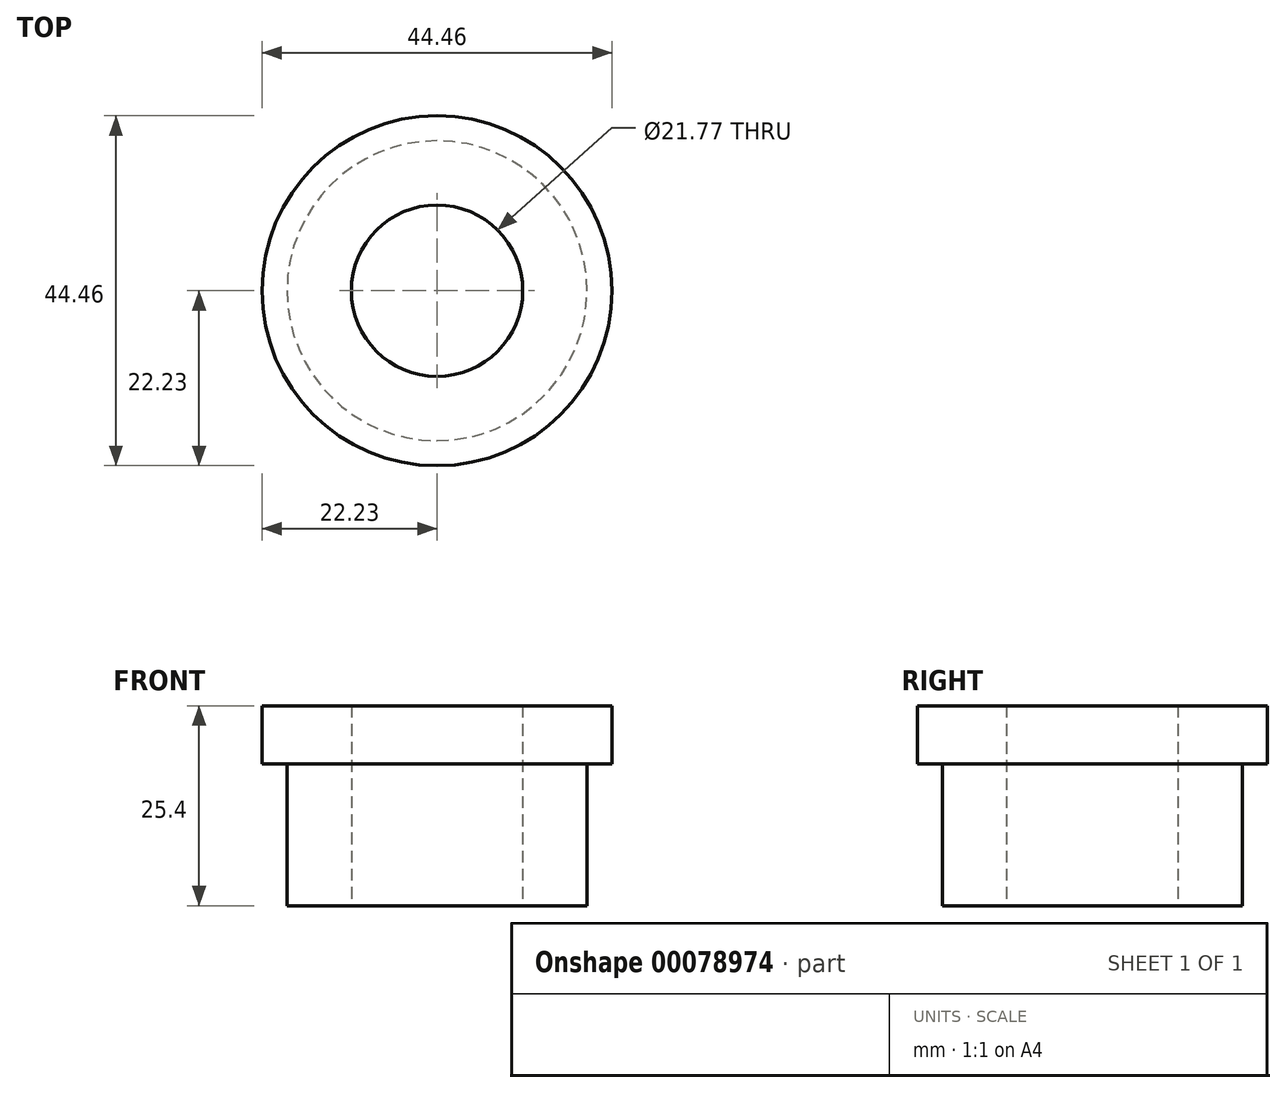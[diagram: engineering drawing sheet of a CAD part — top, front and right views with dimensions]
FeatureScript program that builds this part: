
annotation { "Feature Type Name" : "Feature", "Feature Type Description" : "" }
export const myFeature = defineFeature(function(context is Context, id is Id, definition is map)
    precondition{}
    {
        {
            var Q0;
            Q0=qCreatedBy(makeId("Front.planeOp"),FACE);
            var sketch = newSketch(context, id + "F0", { "sketchPlane" : qUnion([Q0])});
            skLineSegment(sketch, "E0", {"start": v(19.05, 0) * mm, "end": v(19.05, 18.04) * mm});
            skLineSegment(sketch, "E1", {"start": v(19.05, 18.04) * mm, "end": v(22.23, 18.04) * mm});
            skLineSegment(sketch, "E2", {"start": v(22.23, 18.04) * mm, "end": v(22.23, 25.4) * mm});
            skLineSegment(sketch, "E3", {"start": v(22.23, 25.4) * mm, "end": v(10.89, 25.4) * mm});
            skLineSegment(sketch, "E4", {"start": v(10.89, 25.4) * mm, "end": v(10.89, 0) * mm});
            skLineSegment(sketch, "E5", {"start": v(10.89, 0) * mm, "end": v(19.05, 0) * mm});
            skLineSegment(sketch, "E6", {"start": v(0, 0) * mm, "end": v(0, 26.24) * mm, "construction": true});
            skSolve(sketch);
        }
        {
            var Q0;
            Q0 = qSketchRegion(id + "F0", true);
            var Q1;
            Q1=sQuery(id+"F0.wireOp",EDGE,"E6");
            revolve(context, id + "F1", {"entities" : qUnion([Q0]), "axis" : qUnion([Q1]), "revolveType" : RevolveType.FULL});
        }
    });
